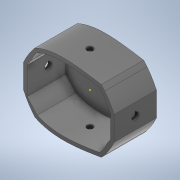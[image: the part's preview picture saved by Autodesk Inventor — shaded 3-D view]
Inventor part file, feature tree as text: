
AUTODESK INVENTOR PART (.ipt)
format: ipt  version: 2021.1 (Build 251245010, 245A)  size: 226,304 bytes
history: native  units: mm
features: extrude x4, sketch x3, plane x3, mirror x1
ambient origin geometry x8: Origin, YZ Plane, XZ Plane, XY Plane, X Axis, Y Axis, Z Axis, Center Point
bodies: Solid1 (feature_tree)
feature tree (11):
  sketch  "Sketch1"  dims[d1=70.0mm d2=70.0mm]
  sketch  "Sketch2"  dims[d3=0.0mm d4=6.0mm]
  extrude  "Extrusion1"  Depth=70.0mm
  extrude  "Extrusion2"  Depth=6.0mm
  plane  "Work Plane1"
  extrude  "Extrusion3"  TaperAngle=0.0deg  [1 undecoded]
  plane  "Work Plane2"
  sketch  "Sketch5"  dims[d5=64.0mm d6=0.0mm d7=60.0mm d9=300.0mm d10=0.0mm d11=49.151954mm d12=49.152mm d13=10.0mm d14=10.0mm d15=20.0mm d16=0.0mm d19=40.0mm d20=6.0mm d21=6.0mm]
  mirror  "Mirror1"
  plane  "Work Plane3"
  extrude  "Extrusion4"  Depth=60.0mm
note: 1 required parameter value undecoded (feature->parameter linkage not recoverable at this tier; creation-order binding heuristic only, values carry confidence <= 0.55)
